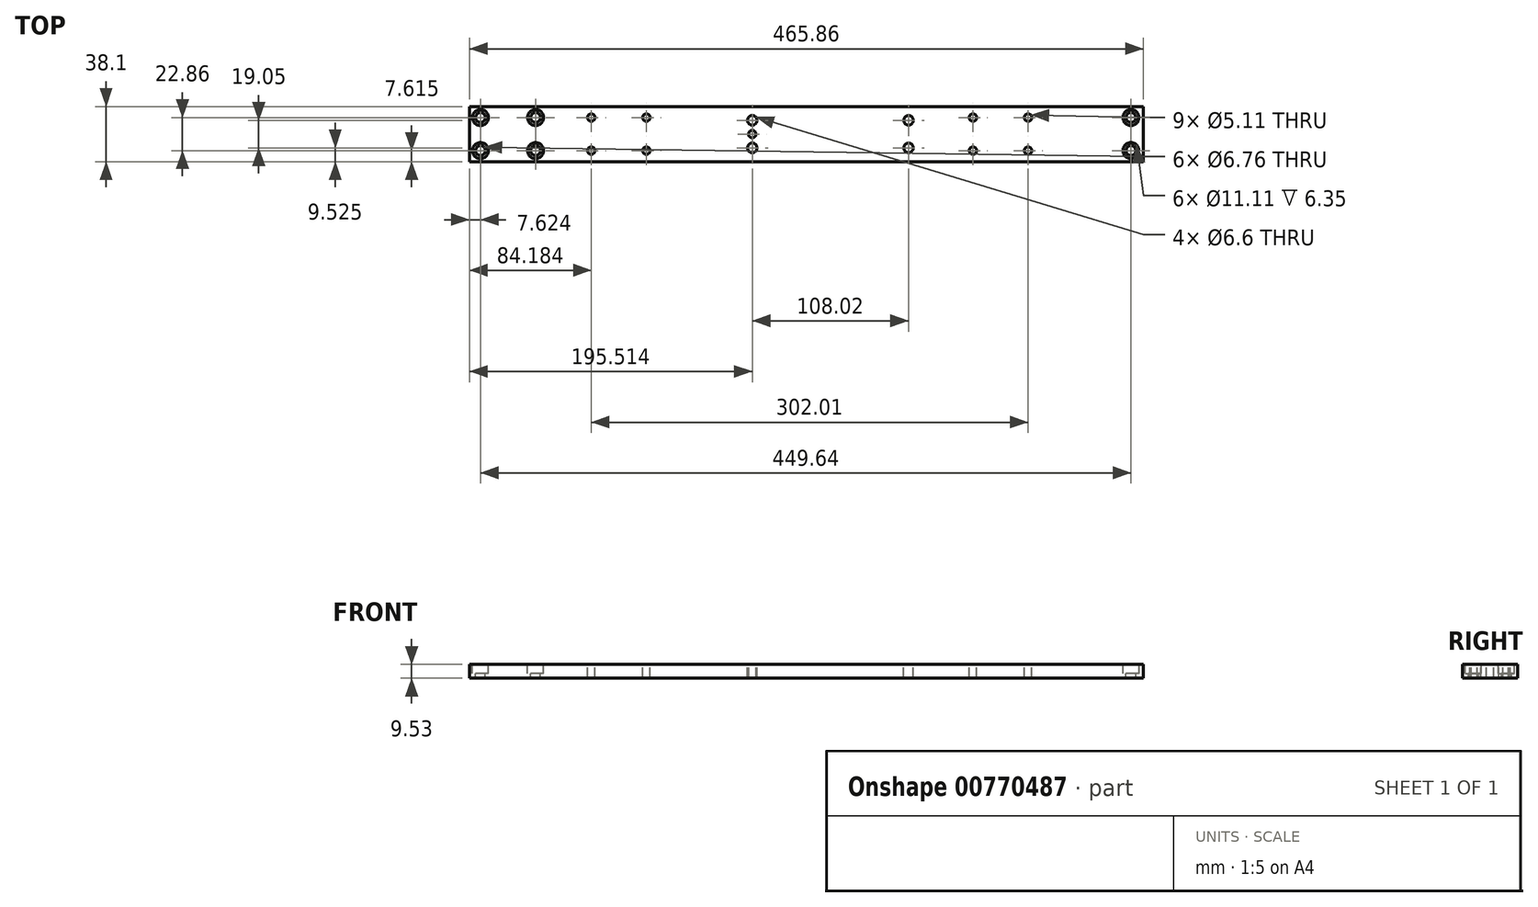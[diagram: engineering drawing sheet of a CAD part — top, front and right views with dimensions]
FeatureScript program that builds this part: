
annotation { "Feature Type Name" : "Feature", "Feature Type Description" : "" }
export const myFeature = defineFeature(function(context is Context, id is Id, definition is map)
    precondition{}
    {
        {
            var Q0;
            Q0=qCreatedBy(makeId("Top.planeOp"),FACE);
            var sketch = newSketch(context, id + "F0", { "sketchPlane" : qUnion([Q0])});
            skLineSegment(sketch, "E0.bottom", {"start": v(-227.27, -29.63) * mm, "end": v(238.6, -29.63) * mm});
            skLineSegment(sketch, "E0.top", {"start": v(-227.27, -67.73) * mm, "end": v(238.6, -67.73) * mm});
            skLineSegment(sketch, "E0.left", {"start": v(-227.27, -29.63) * mm, "end": v(-227.27, -67.73) * mm});
            skLineSegment(sketch, "E0.right", {"start": v(238.6, -29.63) * mm, "end": v(238.6, -67.73) * mm});
            skSolve(sketch);
        }
        {
            var Q0;
            Q0 = qSketchRegion(id + "F0", true);
            extrude(context, id + "F1", {"entities" : qUnion([Q0]), "depth" : 9.53 * mm, "offsetDistance" : 25 * mm});
        }
        {
            var Q0;
            Q0=makeQuery(id+"F1.opExtrude","CAP_FACE",FACE,{"disambiguationData":[OSD([sQuery(id+"F0.wireOp",EDGE,"E0.bottom"),sQuery(id+"F0.wireOp",EDGE,"E0.top"),sQuery(id+"F0.wireOp",EDGE,"E0.left"),sQuery(id+"F0.wireOp",EDGE,"E0.right")])],"isStart":false});
            var sketch = newSketch(context, id + "F2", { "sketchPlane" : qUnion([Q0])});
            skPoint(sketch, "E1", {"position": v(-219.65, -37.25) * mm});
            skPoint(sketch, "E2", {"position": v(-219.65, -60.11) * mm});
            skPoint(sketch, "E3", {"position": v(-181.55, -60.11) * mm});
            skPoint(sketch, "E4", {"position": v(-181.55, -37.25) * mm});
            skPoint(sketch, "E5", {"position": v(-143.09, -37.25) * mm});
            skPoint(sketch, "E6", {"position": v(-104.99, -37.25) * mm});
            skPoint(sketch, "E7", {"position": v(-104.99, -60.11) * mm});
            skPoint(sketch, "E8", {"position": v(-143.09, -60.11) * mm});
            skPoint(sketch, "E9", {"position": v(230, -37.25) * mm});
            skPoint(sketch, "E10", {"position": v(230, -60.11) * mm});
            skPoint(sketch, "E11", {"position": v(158.92, -60.11) * mm});
            skPoint(sketch, "E12", {"position": v(158.92, -37.25) * mm});
            skPoint(sketch, "E13", {"position": v(120.82, -37.25) * mm});
            skPoint(sketch, "E14", {"position": v(120.82, -60.11) * mm});
            skSolve(sketch);
        }
        {
            var Q0;
            Q0=sQuery(id+"F2.wireOp",VERTEX,"E1");
            var Q1;
            Q1=sQuery(id+"F2.wireOp",VERTEX,"E2");
            var Q2;
            Q2=sQuery(id+"F2.wireOp",VERTEX,"E3");
            var Q3;
            Q3=sQuery(id+"F2.wireOp",VERTEX,"E4");
            var Q4;
            Q4=sQuery(id+"F2.wireOp",VERTEX,"E10");
            var Q5;
            Q5=sQuery(id+"F2.wireOp",VERTEX,"E9");
            var Q6;
            Q6=makeQuery(id+"F1.opExtrude","SWEPT_BODY",BODY,{"disambiguationData":[OSD([sQuery(id+"F0.wireOp",EDGE,"E0.bottom"),sQuery(id+"F0.wireOp",EDGE,"E0.top"),sQuery(id+"F0.wireOp",EDGE,"E0.left"),sQuery(id+"F0.wireOp",EDGE,"E0.right")])]});
            hole(context, id + "F3", {"style" : HoleStyle.C_BORE, "endStyle" : HoleEndStyle.THROUGH, "holeDiameter" : 6.76 * mm, "cBoreDiameter" : 11.1 * mm, "cBoreDepth" : 6.35 * mm, "majorDiameter" : 5 * mm, "isTappedThrough" : true, "tappedDepth" : 12 * mm, "tapClearance" : 3, "locations" : qUnion([Q0, Q1, Q2, Q3, Q4, Q5]), "scope" : qUnion([Q6])});
        }
        {
            var Q0;
            Q0=sQuery(id+"F2.wireOp",VERTEX,"E5");
            var Q1;
            Q1=makeQuery(id+"F1.opExtrude","SWEPT_BODY",BODY,{"disambiguationData":[OSD([sQuery(id+"F0.wireOp",EDGE,"E0.bottom"),sQuery(id+"F0.wireOp",EDGE,"E0.top"),sQuery(id+"F0.wireOp",EDGE,"E0.left"),sQuery(id+"F0.wireOp",EDGE,"E0.right")])]});
            hole(context, id + "F4", {"style" : HoleStyle.SIMPLE, "endStyle" : HoleEndStyle.THROUGH, "holeDiameter" : 5.11 * mm, "majorDiameter" : 5 * mm, "isTappedThrough" : true, "tappedDepth" : 12 * mm, "tapClearance" : 3, "locations" : qUnion([Q0]), "scope" : qUnion([Q1])});
        }
        {
            var Q0;
            Q0=sQuery(id+"F2.wireOp",VERTEX,"E8");
            var Q1;
            Q1=sQuery(id+"F2.wireOp",VERTEX,"E7");
            var Q2;
            Q2=sQuery(id+"F2.wireOp",VERTEX,"E6");
            var Q3;
            Q3=sQuery(id+"F2.wireOp",VERTEX,"E5");
            var Q4;
            Q4=sQuery(id+"F2.wireOp",VERTEX,"E13");
            var Q5;
            Q5=sQuery(id+"F2.wireOp",VERTEX,"E12");
            var Q6;
            Q6=sQuery(id+"F2.wireOp",VERTEX,"E11");
            var Q7;
            Q7=sQuery(id+"F2.wireOp",VERTEX,"E14");
            var Q8;
            Q8=makeQuery(id+"F1.opExtrude","SWEPT_BODY",BODY,{"disambiguationData":[OSD([sQuery(id+"F0.wireOp",EDGE,"E0.bottom"),sQuery(id+"F0.wireOp",EDGE,"E0.top"),sQuery(id+"F0.wireOp",EDGE,"E0.left"),sQuery(id+"F0.wireOp",EDGE,"E0.right")])]});
            hole(context, id + "F5", {"style" : HoleStyle.SIMPLE, "endStyle" : HoleEndStyle.THROUGH, "holeDiameter" : 5.11 * mm, "majorDiameter" : 5 * mm, "isTappedThrough" : true, "tappedDepth" : 12 * mm, "tapClearance" : 3, "locations" : qUnion([Q0, Q1, Q2, Q3, Q4, Q5, Q6, Q7]), "scope" : qUnion([Q8])});
        }
        {
            var Q0;
            Q0=makeQuery(id+"F1.opExtrude","CAP_FACE",FACE,{"disambiguationData":[OSD([sQuery(id+"F0.wireOp",EDGE,"E0.bottom"),sQuery(id+"F0.wireOp",EDGE,"E0.top"),sQuery(id+"F0.wireOp",EDGE,"E0.left"),sQuery(id+"F0.wireOp",EDGE,"E0.right")])],"isStart":false});
            var sketch = newSketch(context, id + "F6", { "sketchPlane" : qUnion([Q0])});
            skPoint(sketch, "E15", {"position": v(-31.76, -39.15) * mm});
            skPoint(sketch, "E16", {"position": v(-31.76, -58.2) * mm});
            skPoint(sketch, "E17", {"position": v(76.26, -39.15) * mm});
            skPoint(sketch, "E18", {"position": v(76.26, -58.2) * mm});
            skPoint(sketch, "E19", {"position": v(-31.76, -48.68) * mm});
            skSolve(sketch);
        }
        {
            var Q0;
            Q0=sQuery(id+"F6.wireOp",VERTEX,"E17");
            var Q1;
            Q1=sQuery(id+"F6.wireOp",VERTEX,"E18");
            var Q2;
            Q2=sQuery(id+"F6.wireOp",VERTEX,"E16");
            var Q3;
            Q3=sQuery(id+"F6.wireOp",VERTEX,"E15");
            var Q4;
            Q4=makeQuery(id+"F1.opExtrude","SWEPT_BODY",BODY,{"disambiguationData":[OSD([sQuery(id+"F0.wireOp",EDGE,"E0.bottom"),sQuery(id+"F0.wireOp",EDGE,"E0.top"),sQuery(id+"F0.wireOp",EDGE,"E0.left"),sQuery(id+"F0.wireOp",EDGE,"E0.right")])]});
            hole(context, id + "F7", {"style" : HoleStyle.SIMPLE, "endStyle" : HoleEndStyle.THROUGH, "holeDiameter" : 6.6 * mm, "majorDiameter" : 5 * mm, "isTappedThrough" : true, "tappedDepth" : 12 * mm, "tapClearance" : 3, "locations" : qUnion([Q0, Q1, Q2, Q3]), "scope" : qUnion([Q4])});
        }
        {
            var Q0;
            Q0=sQuery(id+"F6.wireOp",VERTEX,"E19");
            var Q1;
            Q1=makeQuery(id+"F1.opExtrude","SWEPT_BODY",BODY,{"disambiguationData":[OSD([sQuery(id+"F0.wireOp",EDGE,"E0.bottom"),sQuery(id+"F0.wireOp",EDGE,"E0.top"),sQuery(id+"F0.wireOp",EDGE,"E0.left"),sQuery(id+"F0.wireOp",EDGE,"E0.right")])]});
            hole(context, id + "F8", {"style" : HoleStyle.SIMPLE, "endStyle" : HoleEndStyle.THROUGH, "holeDiameter" : 5.11 * mm, "majorDiameter" : 5 * mm, "isTappedThrough" : true, "tappedDepth" : 12 * mm, "tapClearance" : 3, "locations" : qUnion([Q0]), "scope" : qUnion([Q1])});
        }
    });
